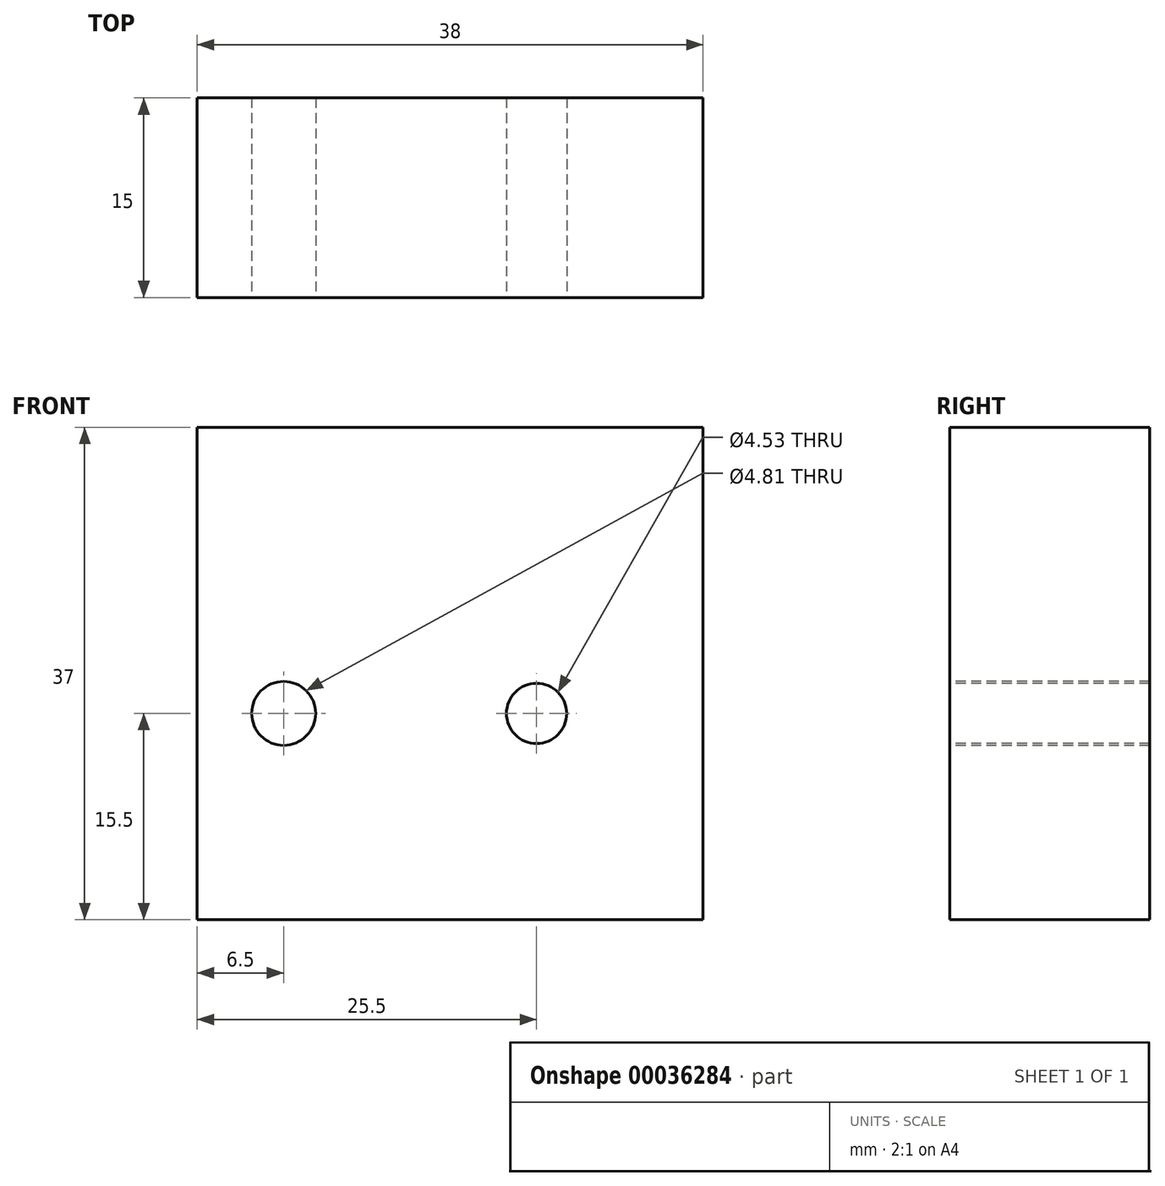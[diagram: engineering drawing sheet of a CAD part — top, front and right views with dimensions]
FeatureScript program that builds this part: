
annotation { "Feature Type Name" : "Feature", "Feature Type Description" : "" }
export const myFeature = defineFeature(function(context is Context, id is Id, definition is map)
    precondition{}
    {
        {
            var Q0;
            Q0=qCreatedBy(makeId("Top.planeOp"),FACE);
            var sketch = newSketch(context, id + "F0", { "sketchPlane" : qUnion([Q0])});
            skLineSegment(sketch, "E0.bottom", {"start": v(0, 0) * mm, "end": v(38, 0) * mm});
            skLineSegment(sketch, "E0.top", {"start": v(0, -15) * mm, "end": v(38, -15) * mm});
            skLineSegment(sketch, "E0.left", {"start": v(0, 0) * mm, "end": v(0, -15) * mm});
            skLineSegment(sketch, "E0.right", {"start": v(38, 0) * mm, "end": v(38, -15) * mm});
            skSolve(sketch);
        }
        {
            var Q0;
            Q0=qSketchRegion(id+"F0",true);
            extrude(context, id + "F1", {"entities" : qUnion([Q0]), "depth" : 37 * mm});
        }
        {
            var Q0;
            Q0=makeQuery(id+"F1.opExtrude","SWEPT_FACE",FACE,{"disambiguationData":[OSD([sQuery(id+"F0.wireOp",EDGE,"E0.top")])]});
            var sketch = newSketch(context, id + "F2", { "sketchPlane" : qUnion([Q0])});
            skCircle(sketch, "E1", {"center": v(6.5, 15.5) * mm, "radius": 2.4 * mm});
            skCircle(sketch, "E2", {"center": v(25.5, 15.5) * mm, "radius": 2.26 * mm});
            skSolve(sketch);
        }
        {
            var Q0;
            Q0=makeQuery(id+"F2.imprint","IMPRINT",FACE,{"disambiguationData":[TD([[makeQuery(id+"F2.imprint","IMPRINT",EDGE,{"derivedFrom":sQuery(id+"F2.wireOp",EDGE,"E1")}),1.0]])]});
            var Q1;
            Q1=makeQuery(id+"F2.imprint","IMPRINT",FACE,{"disambiguationData":[TD([[makeQuery(id+"F2.imprint","IMPRINT",EDGE,{"derivedFrom":sQuery(id+"F2.wireOp",EDGE,"E2")}),1.0]])]});
            extrude(context, id + "F3", {"entities" : qUnion([Q0, Q1]), "operationType" : NewBodyOperationType.REMOVE, "endBound" : BoundingType.THROUGH_ALL, "oppositeDirection" : true, "depth" : 25 * mm});
        }
    });
